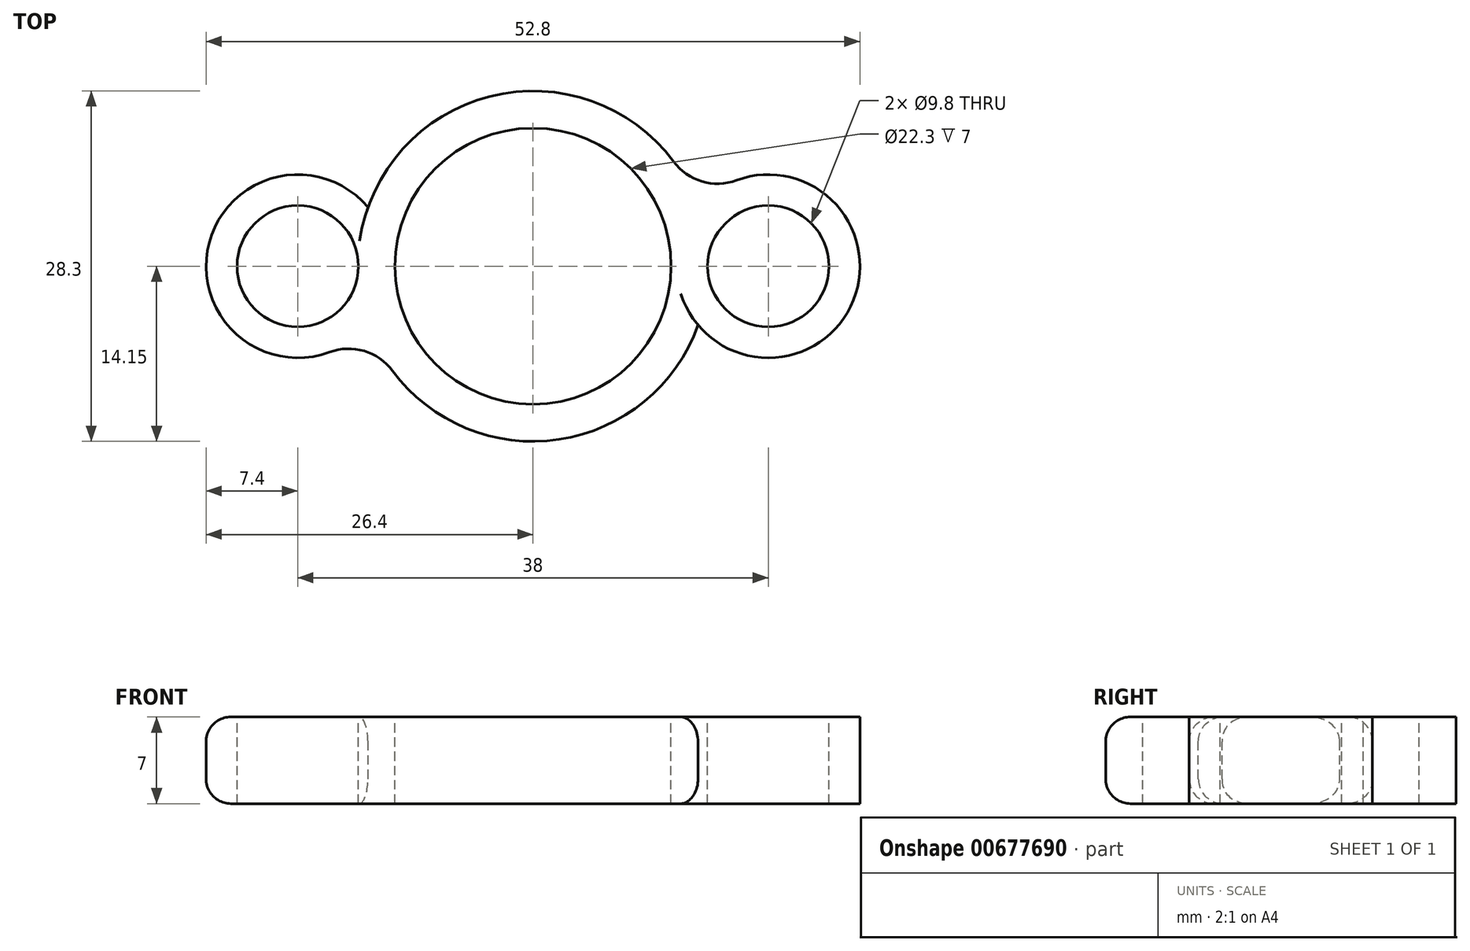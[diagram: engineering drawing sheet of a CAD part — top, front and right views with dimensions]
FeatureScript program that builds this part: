
annotation { "Feature Type Name" : "Feature", "Feature Type Description" : "" }
export const myFeature = defineFeature(function(context is Context, id is Id, definition is map)
    precondition{}
    {
        {
            var Q0;
            Q0=qCreatedBy(makeId("Top.planeOp"),FACE);
            var sketch = newSketch(context, id + "F0", { "sketchPlane" : qUnion([Q0])});
            skCircle(sketch, "E0", {"center": v(0, 0) * mm, "radius": 11.15 * mm});
            skCircle(sketch, "E1", {"center": v(0, 0) * mm, "radius": 14.15 * mm});
            skCircle(sketch, "E2", {"center": v(19, 0) * mm, "radius": 4.9 * mm});
            skPoint(sketch, "E3.center", {"position": v(-3, 0) * mm});
            skCircle(sketch, "E4", {"center": v(19, 0) * mm, "radius": 7.4 * mm});
            skArc(sketch, "E5", {"start": v(11.35, 8.45) * mm, "mid": v(13.64, 6.85) * mm, "end": v(16.43, 6.94) * mm});
            skArc(sketch, "E6.MirrorCS", {"start": v(11.35, -8.45) * mm, "mid": v(13.64, -6.85) * mm, "end": v(16.43, -6.94) * mm});
            skCircle(sketch, "E7.1.0", {"center": v(-19, 0) * mm, "radius": 4.9 * mm});
            skCircle(sketch, "E7.1.1", {"center": v(-19, 0) * mm, "radius": 7.4 * mm});
            skArc(sketch, "E7.1.2", {"start": v(-11.35, -8.45) * mm, "mid": v(-13.64, -6.85) * mm, "end": v(-16.43, -6.94) * mm});
            skArc(sketch, "E7.1.3", {"start": v(-11.35, 8.45) * mm, "mid": v(-13.64, 6.85) * mm, "end": v(-16.43, 6.94) * mm});
            skSolve(sketch);
        }
        {
            var Q0;
            Q0=makeQuery(id+"F0.imprint","IMPRINT",FACE,{"disambiguationData":[TD([[makeQuery(id+"F0.imprint","IMPRINT",EDGE,{"derivedFrom":sQuery(id+"F0.wireOp",EDGE,"E2")}),-1.0]])]});
            var Q1;
            Q1=makeQuery(id+"F0.imprint","IMPRINT",FACE,{"disambiguationData":[TD([[makeQuery(id+"F0.imprint","IMPRINT",EDGE,{"derivedFrom":sQuery(id+"F0.wireOp",EDGE,"E0")}),-1.0]])]});
            var Q2;
            {var subQ1=sQuery(id+"F0.wireOp",EDGE,"E3.1.0");Q2=makeQuery(id+"F0.imprint","IMPRINT",FACE,{"disambiguationData":[TD([[makeQuery(id+"F0.imprint","IMPRINT",EDGE,{"derivedFrom":subQ1}),1.0]])]});}
            var Q3;
            {var subQ2=sQuery(id+"F0.wireOp",EDGE,"E3.1.1");Q3=makeQuery(id+"F0.imprint","IMPRINT",FACE,{"disambiguationData":[TD([[makeQuery(id+"F0.imprint","IMPRINT",EDGE,{"derivedFrom":subQ2}),-1.0]])]});}
            var Q4;
            {var subQ0=sQuery(id+"F0.wireOp",EDGE,"UrDTAnUB-kznT-S6iM-dF8S-AlLEBCoh3Ui7");Q4=makeQuery(id+"F0.imprint","IMPRINT",FACE,{"disambiguationData":[TD([[makeQuery(id+"F0.imprint","IMPRINT",EDGE,{"derivedFrom":subQ0}),1.0]])]});}
            var Q5;
            {var subQ0=sQuery(id+"F0.wireOp",EDGE,"7cddfb9b-9970-48f6-ab0a-d947e09262d6.1.3");Q5=makeQuery(id+"F0.imprint","IMPRINT",FACE,{"disambiguationData":[TD([[makeQuery(id+"F0.imprint","IMPRINT",EDGE,{"derivedFrom":subQ0}),1.0]])]});}
            var Q6;
            {var subQ0=sQuery(id+"F0.wireOp",EDGE,"7cddfb9b-9970-48f6-ab0a-d947e09262d6.1.2");Q6=makeQuery(id+"F0.imprint","IMPRINT",FACE,{"disambiguationData":[TD([[makeQuery(id+"F0.imprint","IMPRINT",EDGE,{"derivedFrom":subQ0}),-1.0]])]});}
            var Q7;
            Q7=makeQuery(id+"F0.imprint","IMPRINT",FACE,{"disambiguationData":[TD([[makeQuery(id+"F0.imprint","IMPRINT",EDGE,{"derivedFrom":sQuery(id+"F0.wireOp",EDGE,"7cddfb9b-9970-48f6-ab0a-d947e09262d6.1.0")}),-1.0]])]});
            var Q8;
            {var subQ0=sQuery(id+"F0.wireOp",EDGE,"i2K6XC5c-Ul34-5Yke-RdwK-Fgtbr8UY5UF6");Q8=makeQuery(id+"F0.imprint","IMPRINT",FACE,{"disambiguationData":[TD([[makeQuery(id+"F0.imprint","IMPRINT",EDGE,{"derivedFrom":subQ0}),-1.0]])]});}
            var Q9;
            {var subQ0=sQuery(id+"F0.wireOp",EDGE,"E7.1.1");var subQ1=sQuery(id+"F0.wireOp",EDGE,"E1");var subQ2=makeQuery(id+"F0.imprint","INTERSECT",VERTEX,{"disambiguationData":[OD(0.0)],"derivedFrom":[subQ1,subQ0]});Q9=makeQuery(id+"F0.imprint","IMPRINT",FACE,{"disambiguationData":[TD([[makeQuery(id+"F0.imprint","IMPRINT",EDGE,{"disambiguationData":[TD([[subQ2,-1.0]])],"derivedFrom":subQ1}),1.0]])]});}
            var Q10;
            {var subQ0=sQuery(id+"F0.wireOp",EDGE,"E7.1.1");var subQ2=sQuery(id+"F0.wireOp",EDGE,"E1");var subQ7=makeQuery(id+"F0.imprint","INTERSECT",VERTEX,{"disambiguationData":[OD(0.0)],"derivedFrom":[subQ2,subQ0]});Q10=makeQuery(id+"F0.imprint","IMPRINT",FACE,{"disambiguationData":[TD([[makeQuery(id+"F0.imprint","IMPRINT",EDGE,{"disambiguationData":[TD([[subQ7,-1.0]])],"derivedFrom":subQ2}),-1.0]])]});}
            var Q11;
            {var subQ0=sQuery(id+"F0.wireOp",EDGE,"E4");var subQ2=sQuery(id+"F0.wireOp",EDGE,"E1");var subQ3=makeQuery(id+"F0.imprint","INTERSECT",VERTEX,{"disambiguationData":[OD(0.0)],"derivedFrom":[subQ2,subQ0]});Q11=makeQuery(id+"F0.imprint","IMPRINT",FACE,{"disambiguationData":[TD([[makeQuery(id+"F0.imprint","IMPRINT",EDGE,{"disambiguationData":[TD([[subQ3,1.0]])],"derivedFrom":subQ2}),-1.0]])]});}
            var Q12;
            {var subQ0=sQuery(id+"F0.wireOp",EDGE,"E6.MirrorCS");Q12=makeQuery(id+"F0.imprint","IMPRINT",FACE,{"disambiguationData":[TD([[makeQuery(id+"F0.imprint","IMPRINT",EDGE,{"derivedFrom":subQ0}),1.0]])]});}
            var Q13;
            {var subQ0=sQuery(id+"F0.wireOp",EDGE,"E5");Q13=makeQuery(id+"F0.imprint","IMPRINT",FACE,{"disambiguationData":[TD([[makeQuery(id+"F0.imprint","IMPRINT",EDGE,{"derivedFrom":subQ0}),-1.0]])]});}
            var Q14;
            {var subQ0=sQuery(id+"F0.wireOp",EDGE,"E7.1.2");Q14=makeQuery(id+"F0.imprint","IMPRINT",FACE,{"disambiguationData":[TD([[makeQuery(id+"F0.imprint","IMPRINT",EDGE,{"derivedFrom":subQ0}),-1.0]])]});}
            var Q15;
            {var subQ0=sQuery(id+"F0.wireOp",EDGE,"E7.1.3");Q15=makeQuery(id+"F0.imprint","IMPRINT",FACE,{"disambiguationData":[TD([[makeQuery(id+"F0.imprint","IMPRINT",EDGE,{"derivedFrom":subQ0}),1.0]])]});}
            extrude(context, id + "F1", {"entities" : qUnion([Q0, Q1, Q2, Q3, Q4, Q5, Q6, Q7, Q8, Q9, Q10, Q11, Q12, Q13, Q14, Q15]), "oppositeDirection" : true, "depth" : 7 * mm, "offsetDistance" : 25 * mm});
        }
        {
            var Q0;
            Q0=makeQuery(id+"F1.opExtrude","CAP_EDGE",EDGE,{"disambiguationData":[OSD([sQuery(id+"F0.wireOp",EDGE,"UrDTAnUB-kznT-S6iM-dF8S-AlLEBCoh3Ui7")])],"isStart":true});
            var Q1;
            Q1=makeQuery(id+"F1.opExtrude","CAP_EDGE",EDGE,{"disambiguationData":[OSD([sQuery(id+"F0.wireOp",EDGE,"i2K6XC5c-Ul34-5Yke-RdwK-Fgtbr8UY5UF6")])],"isStart":false});
            var Q2;
            {var subQ0=sQuery(id+"F0.wireOp",EDGE,"E1");Q2=makeQuery(id+"F1.opExtrude","CAP_EDGE",EDGE,{"disambiguationData":[OSD([subQ0]),TDD([makeQuery(id+"F0.imprint","IMPRINT",EDGE,{"disambiguationData":[TD([[makeQuery(id+"F0.imprint","INTERSECT",VERTEX,{"derivedFrom":[subQ0,sQuery(id+"F0.wireOp",EDGE,"E6.MirrorCS")]}),1.0]])],"derivedFrom":subQ0})])],"isStart":true});}
            var Q3;
            {var subQ0=sQuery(id+"F0.wireOp",EDGE,"E1");Q3=makeQuery(id+"F1.opExtrude","CAP_EDGE",EDGE,{"disambiguationData":[OSD([subQ0]),TDD([makeQuery(id+"F0.imprint","IMPRINT",EDGE,{"disambiguationData":[TD([[makeQuery(id+"F0.imprint","INTERSECT",VERTEX,{"derivedFrom":[subQ0,sQuery(id+"F0.wireOp",EDGE,"E6.MirrorCS")]}),1.0]])],"derivedFrom":subQ0})])],"isStart":false});}
            fillet(context, id + "F2", {"entities" : qUnion([Q0, Q1, Q2, Q3]), "radius" : 2 * mm, "tangentPropagation" : true, "allowEdgeOverflow" : false});
        }
    });
